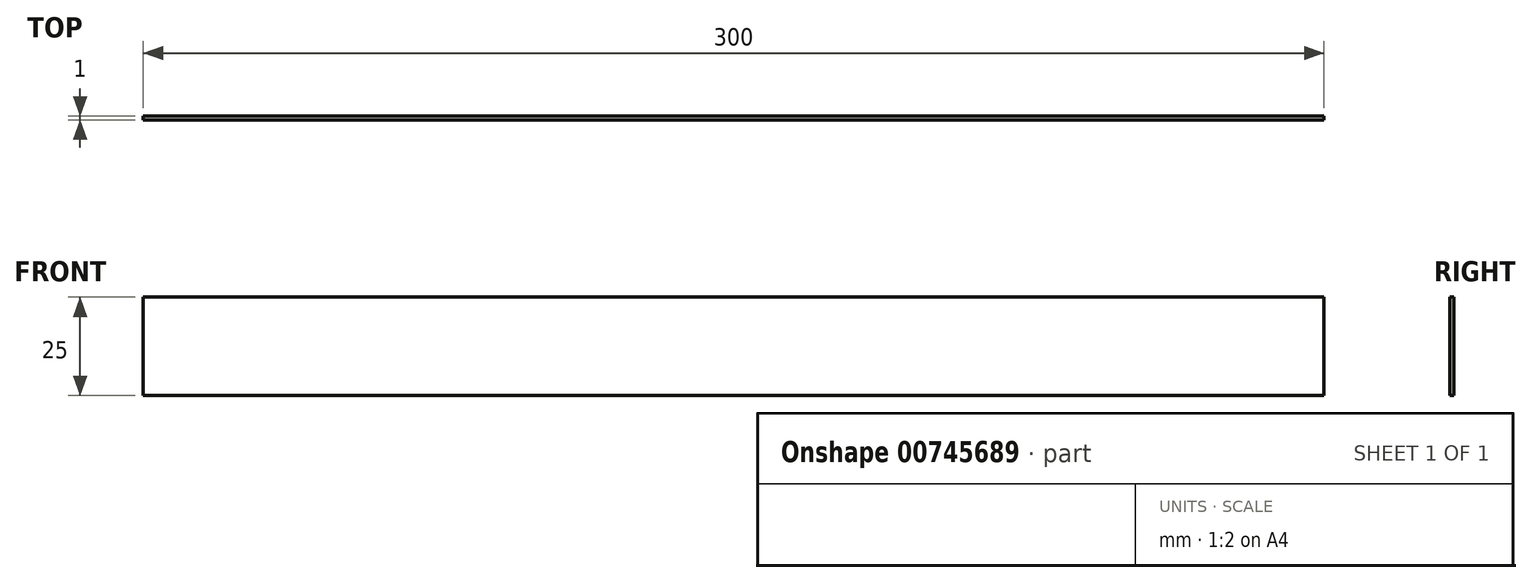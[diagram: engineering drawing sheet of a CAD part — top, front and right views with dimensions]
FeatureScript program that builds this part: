
annotation { "Feature Type Name" : "Feature", "Feature Type Description" : "" }
export const myFeature = defineFeature(function(context is Context, id is Id, definition is map)
    precondition{}
    {
        {
            var Q0;
            Q0=qCreatedBy(makeId("Front.planeOp"),FACE);
            var sketch = newSketch(context, id + "F0", { "sketchPlane" : qUnion([Q0])});
            skLineSegment(sketch, "E0.bottom", {"start": v(150, -12.5) * mm, "end": v(-150, -12.5) * mm});
            skLineSegment(sketch, "E0.top", {"start": v(150, 12.5) * mm, "end": v(-150, 12.5) * mm});
            skLineSegment(sketch, "E0.left", {"start": v(150, -12.5) * mm, "end": v(150, 12.5) * mm});
            skLineSegment(sketch, "E0.right", {"start": v(-150, -12.5) * mm, "end": v(-150, 12.5) * mm});
            skPoint(sketch, "E0.middle", {"position": v(0, 0) * mm});
            skSolve(sketch);
        }
        {
            var Q0;
            Q0 = qSketchRegion(id + "F0", true);
            extrude(context, id + "F1", {"entities" : qUnion([Q0]), "depth" : 1 * mm, "offsetDistance" : 25.4 * mm});
        }
    });
